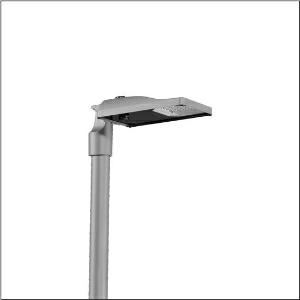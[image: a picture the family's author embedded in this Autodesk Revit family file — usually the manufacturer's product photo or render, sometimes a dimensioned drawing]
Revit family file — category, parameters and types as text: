
# Revit family: streetlight_sl_31_micro___pl52_5xh5h31t08da_3d46
name_source: partatom
category: Lighting Fixtures
units: mm (PartAtom-declared; Revit-internal decimal feet)

## family parameters
Cut with Voids When Loaded = No
Host = Face
Light Source = No
Part Type = Normal
Room Calculation Point = No
Round Connector Dimension = Use Diameter
Shared = No

## types (1)
- --- (1 x LED, 4850 lm, 37.7 W, 3000K)
    Apparent Load = 38 VA
    CIE Flux Codes = 27 59 98 100 100
    Color Rendering = 70
    Color Temperature = 3000K
    Default Elevation = 1800 mm
    Description = Streetlight SL 31 micro D4i, Desk-Remote mast luminaire for post-top, side-entry; light control with lens of PMMA; light distribution: PL52, direct asymmetric distribution, for standard-compliant lighting for roads and squares; LED: luminous flux: 4.850lm, light colour: 730, colour temperature: 3000K; luminous efficacy: 128,6lm/W; control: pre-setting: logarithmic dimming characteristic, flexible luminous flux parameterisation, time-dependent luminous flux control, constant luminous flux control, power reduction, intelligent temperature release in ECG and LED module, overheat protection; luminaire housing, of diecast aluminium, Siteco® metallic grey (DB 702S), corrosivity category C5 high according to DIN EN ISO 12944; cover of toughened safety glass, transparent, opened without tools; mast flange of diecast aluminium, Siteco® metallic grey (DB 702S), spigot size: 76/60mm, mast flange included unmounted; with cable H07RN-F 2x 1.5mm², cable length: 6,5m, connection cable pre-assembled; mains connection: 220..240V, AC, 50/60Hz; power consumption (at start of service life): 37,7W / (at end of service life): 40,9W / (with reduced operation 50%): 16,3W; protection rating (complete): IP66; insulation class (complete): insulation class II (safety insulation); impact resistance: IK09; certification: CE, ENEC, ENEC+, VDE, UKCA, ZD4i; permissible operating ambient temperature for outdoor applications: -40..+50°C; packaging unit: 1 piece

Light Distribution: PL52
    Height = 76 mm
    Lamp = 1 x LED
    Lamp Light Flux = 4850 lm
    Lamp Power = 37.7 W
    Lamp count = 1
    Length = 467 mm
    Luminous efficacy = 129 lm/W
    Manufacturer = Siteco
    ModVariant = No
    Model = 5XH5H31T08DA
    Number of Poles = 1
    OnlyDefault = Yes
    Power Factor = 1
    Product Name = Streetlight SL 31 micro | PL52
    Product group = mast luminaire | pylon top
    ProductGroupID = 6100
    Protection Class = Protection class II
    Protection Degree = IP 66
    RLX_Detail_Level = 1
    RLX_Emergency_Light_Flux = 0 lm
    RLX_Emergency_Type = 0
    RLX_Emergency_Type_DB = No
    RlxData = <blob elided: 53877 chars, md5=ea2588d2>
    Socket = socket
    Standby Power = 0 W
    System Light Flux = 4850 lm
    System Power = 38 W
    Type Comments = factory setting: luminous flux: 100 % | dim-lin: 254 | 745 mA
    Type Image = l_1300315.jpg
    URL = http://relux.com
    VarID = @adj_057901
    Voltage = 0 V
    Weight = 0.00 kg
    Width = 265 mm

## geometry (parser evidence)
native form markers: Blend x4, Sweep x13
no freeform markers — native parametric forms only
